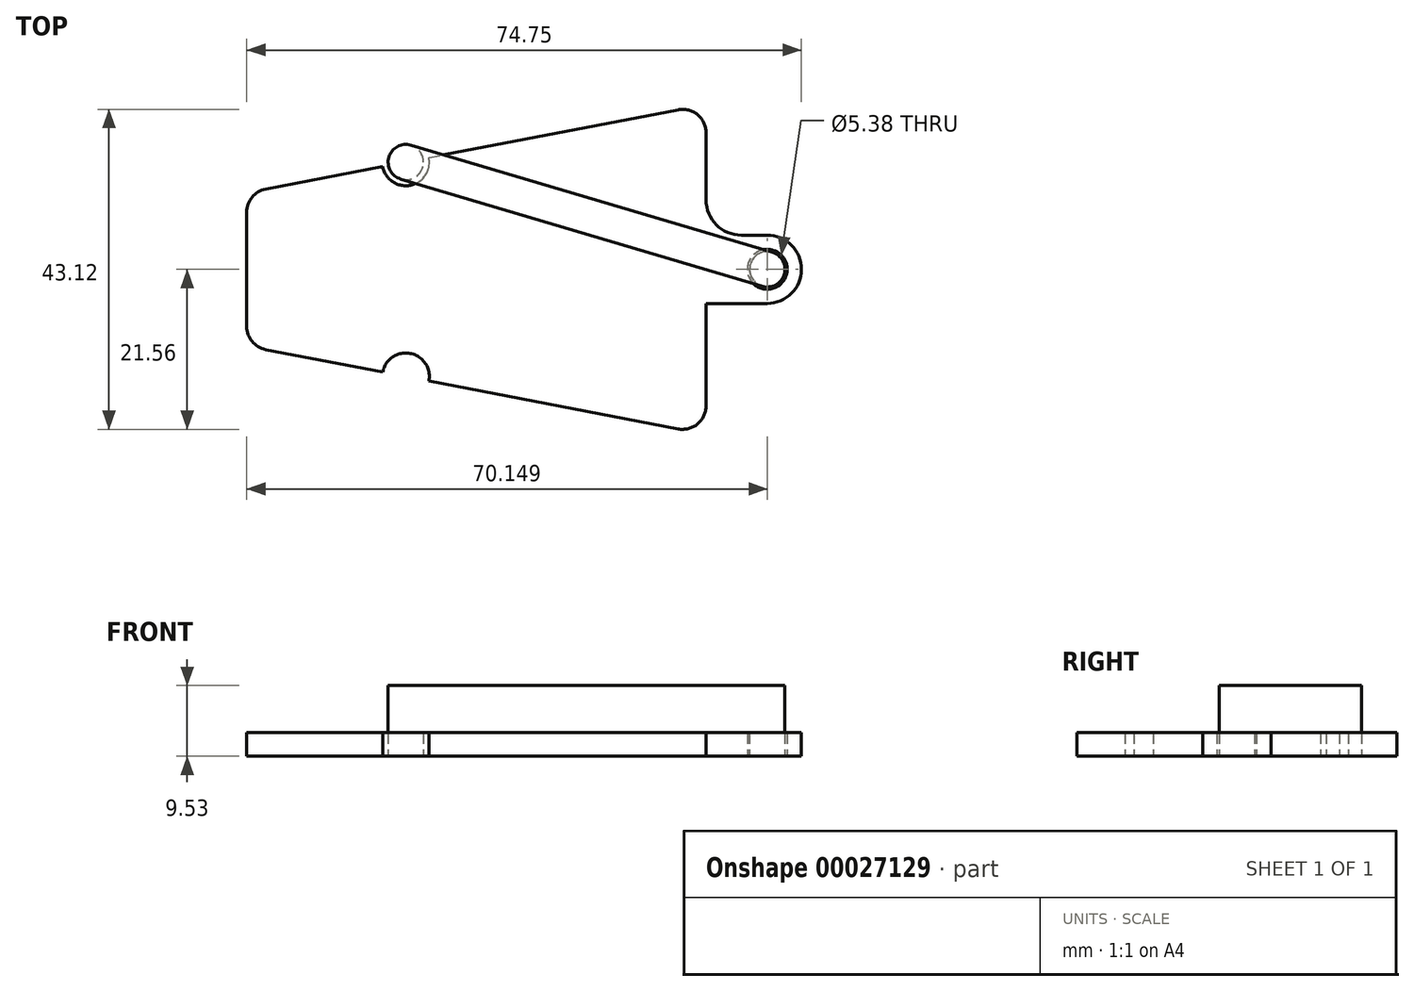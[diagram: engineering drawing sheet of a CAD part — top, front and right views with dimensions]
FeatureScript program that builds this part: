
annotation { "Feature Type Name" : "Feature", "Feature Type Description" : "" }
export const myFeature = defineFeature(function(context is Context, id is Id, definition is map)
    precondition{}
    {
        {
            var Q0;
            Q0=qCreatedBy(makeId("Top.planeOp"),FACE);
            var sketch = newSketch(context, id + "F0", { "sketchPlane" : qUnion([Q0])});
            skLineSegment(sketch, "E0", {"start": v(0, -10.32) * mm, "end": v(0, 10.32) * mm});
            skLineSegment(sketch, "E1", {"start": v(0, 10.32) * mm, "end": v(61.91, 22.23) * mm});
            skLineSegment(sketch, "E2", {"start": v(61.91, 22.23) * mm, "end": v(61.91, -22.23) * mm});
            skLineSegment(sketch, "E3", {"start": v(61.91, -22.23) * mm, "end": v(0, -10.32) * mm});
            skSolve(sketch);
        }
        {
            var Q0;
            Q0=makeQuery(id+"F0.imprint","IMPRINT",FACE,{"disambiguationData":[TD([[makeQuery(id+"F0.imprint","IMPRINT",EDGE,{"derivedFrom":sQuery(id+"F0.wireOp",EDGE,"E0")}),-1.0]])]});
            extrude(context, id + "F1", {"entities" : qUnion([Q0]), "depth" : 3.17 * mm});
        }
        {
            var Q0;
            Q0=qCreatedBy(makeId("Top.planeOp"),FACE);
            var sketch = newSketch(context, id + "F2", { "sketchPlane" : qUnion([Q0])});
            skArc(sketch, "E4", {"start": v(70.15, -4.6) * mm, "mid": v(74.75, 0) * mm, "end": v(70.15, 4.6) * mm});
            skCircle(sketch, "E5", {"center": v(70.15, 0) * mm, "radius": 2.69 * mm});
            skLineSegment(sketch, "E6", {"start": v(70.15, 4.6) * mm, "end": v(61.91, 4.6) * mm});
            skLineSegment(sketch, "E7", {"start": v(70.15, -4.6) * mm, "end": v(61.91, -4.6) * mm});
            skLineSegment(sketch, "E8.0", {"start": v(61.91, 22.23) * mm, "end": v(61.91, -22.23) * mm, "construction": true});
            skLineSegment(sketch, "E9", {"start": v(61.91, -4.6) * mm, "end": v(61.91, 4.6) * mm});
            skSolve(sketch);
        }
        {
            var Q0;
            Q0=makeQuery(id+"F2.imprint","IMPRINT",FACE,{"disambiguationData":[TD([[makeQuery(id+"F2.imprint","IMPRINT",EDGE,{"derivedFrom":sQuery(id+"F2.wireOp",EDGE,"E4")}),1.0]])]});
            extrude(context, id + "F3", {"entities" : qUnion([Q0]), "operationType" : NewBodyOperationType.ADD, "depth" : 3.17 * mm});
        }
        {
            var Q0;
            Q0=qCreatedBy(makeId("Top.planeOp"),FACE);
            var sketch = newSketch(context, id + "F4", { "sketchPlane" : qUnion([Q0])});
            skLineSegment(sketch, "E10.0", {"start": v(0, 10.32) * mm, "end": v(61.91, 22.23) * mm, "construction": true});
            skLineSegment(sketch, "E11.0", {"start": v(61.91, -22.23) * mm, "end": v(0, -10.32) * mm, "construction": true});
            skCircle(sketch, "E12.0", {"center": v(70.15, 0) * mm, "radius": 2.69 * mm, "construction": true});
            skCircle(sketch, "E13", {"center": v(70.15, 0) * mm, "radius": 50.8 * mm, "construction": true});
            skCircle(sketch, "E14", {"center": v(21.45, 14.44) * mm, "radius": 3.18 * mm});
            skCircle(sketch, "E15", {"center": v(21.45, -14.44) * mm, "radius": 3.18 * mm});
            skSolve(sketch);
        }
        {
            var Q0;
            Q0 = qSketchRegion(id + "F4", true);
            extrude(context, id + "F5", {"entities" : qUnion([Q0]), "operationType" : NewBodyOperationType.REMOVE, "endBound" : BoundingType.THROUGH_ALL, "depth" : 25.4 * mm});
        }
        {
            var Q0;
            Q0=makeQuery(id+"F3.opExtrude","SWEPT_EDGE",EDGE,{"disambiguationData":[OSD([sQuery(id+"F2.wireOp",EDGE,"E7"),sQuery(id+"F2.wireOp",EDGE,"E9")])]});
            var Q1;
            Q1=makeQuery(id+"F3.opExtrude","SWEPT_EDGE",EDGE,{"disambiguationData":[OSD([sQuery(id+"F2.wireOp",EDGE,"E6"),sQuery(id+"F2.wireOp",EDGE,"E9")])]});
            fillet(context, id + "F6", {"entities" : qUnion([Q0, Q1]), "radius" : 4.76 * mm, "tangentPropagation" : true, "allowEdgeOverflow" : false});
        }
        {
            var Q0;
            Q0=makeQuery(id+"F1.opExtrude","SWEPT_EDGE",EDGE,{"disambiguationData":[OSD([sQuery(id+"F0.wireOp",EDGE,"E1"),sQuery(id+"F0.wireOp",EDGE,"E2")])]});
            var Q1;
            Q1=makeQuery(id+"F1.opExtrude","SWEPT_EDGE",EDGE,{"disambiguationData":[OSD([sQuery(id+"F0.wireOp",EDGE,"E2"),sQuery(id+"F0.wireOp",EDGE,"E3")])]});
            var Q2;
            Q2=makeQuery(id+"F1.opExtrude","SWEPT_EDGE",EDGE,{"disambiguationData":[OSD([sQuery(id+"F0.wireOp",EDGE,"E0"),sQuery(id+"F0.wireOp",EDGE,"E3")])]});
            var Q3;
            Q3=makeQuery(id+"F1.opExtrude","SWEPT_EDGE",EDGE,{"disambiguationData":[OSD([sQuery(id+"F0.wireOp",EDGE,"E0"),sQuery(id+"F0.wireOp",EDGE,"E1")])]});
            fillet(context, id + "F7", {"entities" : qUnion([Q0, Q1, Q2, Q3]), "radius" : 3.17 * mm, "tangentPropagation" : true, "allowEdgeOverflow" : false});
        }
        {
            var Q0;
            Q0=makeQuery(id+"F3.boolean.opBoolean","MERGE",FACE,{"derivedFrom":[makeQuery(id+"F1.opExtrude","CAP_FACE",FACE,{"disambiguationData":[OSD([sQuery(id+"F0.wireOp",EDGE,"E0"),sQuery(id+"F0.wireOp",EDGE,"E1"),sQuery(id+"F0.wireOp",EDGE,"E2"),sQuery(id+"F0.wireOp",EDGE,"E3")])],"isStart":false}),makeQuery(id+"F3.opExtrude","CAP_FACE",FACE,{"disambiguationData":[OSD([sQuery(id+"F2.wireOp",EDGE,"E4"),sQuery(id+"F2.wireOp",EDGE,"E5"),sQuery(id+"F2.wireOp",EDGE,"E6"),sQuery(id+"F2.wireOp",EDGE,"E7"),sQuery(id+"F2.wireOp",EDGE,"E9")])],"isStart":false})]});
            var sketch = newSketch(context, id + "F8", { "sketchPlane" : qUnion([Q0])});
            skArc(sketch, "E16.0", {"start": v(24.56, 15.04) * mm, "mid": v(22.05, 11.33) * mm, "end": v(18.33, 13.84) * mm, "construction": true});
            skCircle(sketch, "E17.0", {"center": v(70.15, 0) * mm, "radius": 2.69 * mm, "construction": true});
            skArc(sketch, "E18", {"start": v(22.12, 16.73) * mm, "mid": v(19.16, 15.12) * mm, "end": v(20.77, 12.16) * mm});
            skArc(sketch, "E19", {"start": v(69.47, -2.28) * mm, "mid": v(72.43, -0.68) * mm, "end": v(70.83, 2.28) * mm});
            skLineSegment(sketch, "E20", {"start": v(22.12, 16.73) * mm, "end": v(70.83, 2.28) * mm});
            skLineSegment(sketch, "E21.trimOffspring", {"start": v(20.77, 12.16) * mm, "end": v(69.47, -2.28) * mm});
            skSolve(sketch);
        }
        {
            var Q0;
            {var subQ0=sQuery(id+"F2.wireOp",EDGE,"E5");var subQ1=makeQuery(id+"F3.opExtrude","CAP_EDGE",EDGE,{"disambiguationData":[OSD([subQ0])],"isStart":false});var subQ4=sQuery(id+"F8.wireOp",EDGE,"E20");var subQ5=makeQuery(id+"F8.imprint","INTERSECT",VERTEX,{"derivedFrom":[subQ1,subQ4]});Q0=makeQuery(id+"F8.imprint","IMPRINT",FACE,{"disambiguationData":[TD([[makeQuery(id+"F8.imprint","IMPRINT",EDGE,{"disambiguationData":[TD([[subQ5,-1.0]])],"derivedFrom":subQ1}),-1.0]])]});}
            var Q1;
            {var subQ12=sQuery(id+"F8.wireOp",EDGE,"E18");Q1=makeQuery(id+"F8.imprint","IMPRINT",FACE,{"disambiguationData":[TD([[makeQuery(id+"F8.imprint","IMPRINT",EDGE,{"derivedFrom":subQ12}),1.0]])]});}
            var Q2;
            Q2 = qSketchRegion(id + "F8", true);
            extrude(context, id + "F9", {"entities" : qUnion([Q0, Q1, Q2]), "depth" : 6.35 * mm});
        }
        {
            var Q0;
            Q0=makeQuery(id+"F9.opExtrude","CAP_FACE",FACE,{"disambiguationData":[OSD([sQuery(id+"F8.wireOp",EDGE,"E18"),sQuery(id+"F8.wireOp",EDGE,"E19"),sQuery(id+"F8.wireOp",EDGE,"E20"),sQuery(id+"F8.wireOp",EDGE,"E21.trimOffspring")])],"isStart":true});
            var sketch = newSketch(context, id + "F10", { "sketchPlane" : qUnion([Q0])});
            skCircle(sketch, "E22", {"center": v(70.15, 0) * mm, "radius": 2.38 * mm});
            skCircle(sketch, "E23", {"center": v(21.45, -14.44) * mm, "radius": 2.38 * mm});
            skSolve(sketch);
        }
        {
            var Q0;
            Q0 = qSketchRegion(id + "F10", true);
            extrude(context, id + "F11", {"entities" : qUnion([Q0]), "operationType" : NewBodyOperationType.ADD, "depth" : 3.17 * mm});
        }
    });
